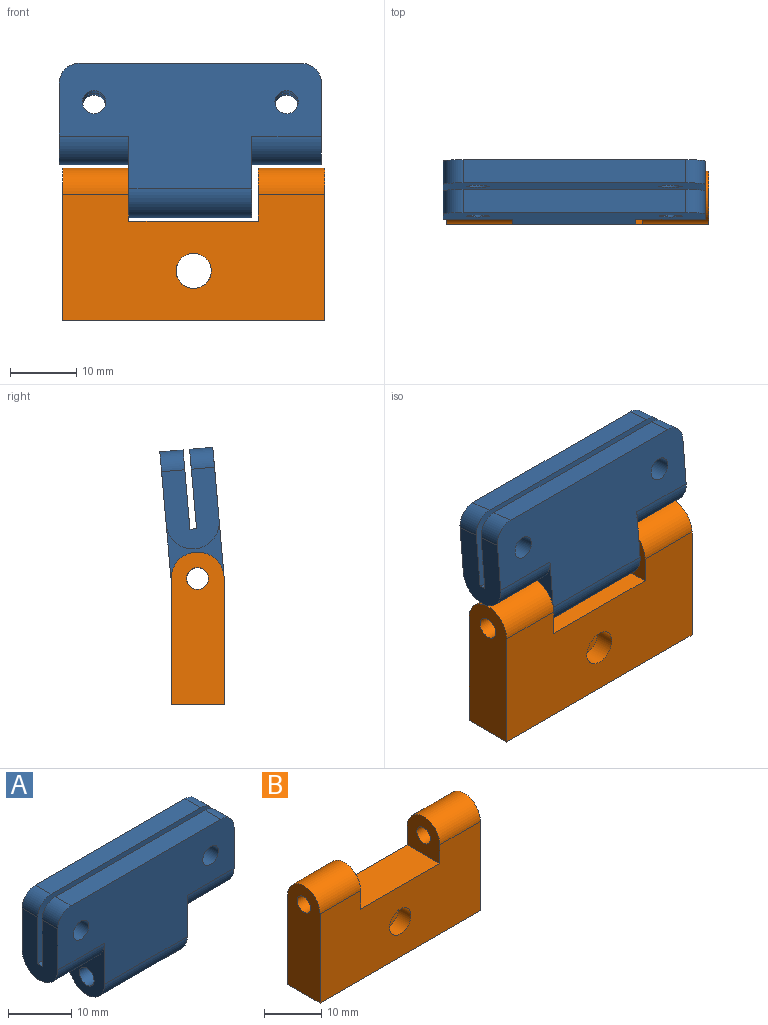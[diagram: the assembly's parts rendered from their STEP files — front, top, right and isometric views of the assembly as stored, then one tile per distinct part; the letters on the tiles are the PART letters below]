
ASSEMBLY  parts=2 mates=1
PART A: 23 faces, bbox 39.5x8x23 mm
  f0: plane 33.5x3.5mm, normal (0,0,1), area 117.2mm2, adj f2,f11,f16,f17
  f1: plane 12x8mm, normal (1,0,0), area 80.1mm2, adj f2,f4,f9,f11,f12,f13,f15,f17
  f2: plane 39.5x19mm, normal (0,1,0), area 559.4mm2, adj f0,f1,f3,f5,f6,f7,f9,f10
  f3: plane 12x8mm, normal (-1,0,0), area 55.4mm2, adj f2,f4,f6,f10,f22
  f4: plane 39.5x19mm, normal (0,-1,0), area 559.4mm2, adj f1,f3,f5,f6,f7,f8,f9,f10
  f5: plane 12x8mm, normal (1,0,0), area 55.4mm2, adj f2,f4,f6,f9,f22
  f6: cylinder r=4mm len=18.5mm, axis (-1,0,0), area 232.5mm2, adj f2,f3,f4,f5
  f7: plane 12x8mm, normal (-1,0,0), area 80.1mm2, adj f2,f4,f10,f11,f12,f13,f14,f16
  f8: plane 33.5x3.5mm, normal (0,0,1), area 117.3mm2, adj f4,f12,f14,f15
  f9: cylinder r=4mm len=10.5mm, axis (1,0,0), area 131.9mm2, adj f1,f2,f4,f5
  f10: cylinder r=4mm len=10.5mm, axis (1,0,0), area 131.9mm2, adj f2,f3,f4,f7
  f11: plane 39.5x12mm, normal (0,-1,0), area 450.9mm2, adj f0,f1,f7,f13,f16,f17,f20,f21
  f12: plane 39.5x12mm, normal (0,1,0), area 450.9mm2, adj f1,f7,f8,f13,f14,f15,f18,f19
  f13: plane 39.5x1mm, normal (0,0,1), area 39.5mm2, adj f1,f7,f11,f12
  f14: cylinder r=3mm len=3.5mm, axis (0,1,0), area 16.5mm2, adj f4,f7,f8,f12
  f15: cylinder r=3mm len=3.5mm, axis (0,-1,0), area 16.5mm2, adj f1,f4,f8,f12
  f16: cylinder r=3mm len=3.5mm, axis (0,1,0), area 16.5mm2, adj f0,f2,f7,f11
  f17: cylinder r=3mm len=3.5mm, axis (0,-1,0), area 16.5mm2, adj f0,f1,f2,f11
  f18: cylinder r=1.75mm len=3.5mm, axis (0,-1,0), area 38.5mm2, adj f4,f12
  f19: cylinder r=1.75mm len=3.5mm, axis (0,-1,0), area 38.5mm2, adj f4,f12
  f20: cylinder r=1.75mm len=3.5mm, axis (0,-1,0), area 38.5mm2, adj f2,f11
  f21: cylinder r=1.75mm len=3.5mm, axis (0,-1,0), area 38.5mm2, adj f2,f11
  f22: cylinder r=1.65mm len=18.5mm, axis (1,0,0), area 191.8mm2, adj f3,f5
PART B: 19 faces, bbox 39.5x8x23 mm
  f0: plane 19.5x8mm, normal (0,0,1), area 156mm2, adj f6,f7,f13,f14
  f1: plane 39.5x8mm, normal (0,0,-1), area 249mm2, adj f3,f5,f6,f7,f8,f9,f10,f11
  f2: cylinder r=2.65mm len=5.3mm, axis (0,1,0), area 50mm2, adj f6,f8
  f3: plane 23x8mm, normal (1,0,0), area 168.6mm2, adj f1,f6,f7,f15,f17
  f4: cylinder r=2.65mm len=5.3mm, axis (0,1,0), area 50mm2, adj f7,f10
  f5: plane 23x8mm, normal (-1,0,0), area 168.6mm2, adj f1,f6,f7,f16,f18
  f6: plane 39.5x19mm, normal (0,-1,0), area 650.4mm2, adj f0,f1,f2,f3,f5,f13,f14,f15
  f7: plane 39.5x19mm, normal (0,1,0), area 650.4mm2, adj f0,f1,f3,f4,f5,f13,f14,f15
  f8: plane 33.5x12mm, normal (0,1,0), area 379.9mm2, adj f1,f2,f9,f11,f12
  f9: plane 12x2mm, normal (1,0,0), area 24mm2, adj f1,f8,f10,f12
  f10: plane 33.5x12mm, normal (0,-1,0), area 379.9mm2, adj f1,f4,f9,f11,f12
  f11: plane 12x2mm, normal (-1,0,0), area 24mm2, adj f1,f8,f10,f12
  f12: plane 33.5x2mm, normal (0,0,-1), area 67mm2, adj f8,f9,f10,f11
  f13: plane 8x8mm, normal (1,0,0), area 48.6mm2, adj f0,f6,f7,f16,f18
  f14: plane 8x8mm, normal (-1,0,0), area 48.6mm2, adj f0,f6,f7,f15,f17
  f15: cylinder r=4mm len=10mm, axis (1,0,0), area 125.7mm2, adj f3,f6,f7,f14
  f16: cylinder r=4mm len=10mm, axis (-1,0,0), area 125.7mm2, adj f5,f6,f7,f13
  f17: cylinder r=1.65mm len=10mm, axis (1,0,0), area 103.7mm2, adj f3,f14
  f18: cylinder r=1.65mm len=10mm, axis (1,0,0), area 103.7mm2, adj f5,f13
PLACE A rot(axis=(-1,0,0),5deg) t=(-0.5,1.66,-4.59)mm
PLACE B t=(0,2.68,-4.29)mm
MATE revolute A.f22 <-> B.f17  axis (1,0,0) through (-9.75,-1.32,7.21)mm
